# Revit family: ShowerTray_70x70cm_Vitra_ArkitektSeries_5735L003-0578
name_source: partatom
category: Plumbing Fixtures
revit_build: Autodesk Revit 2017 (Build: 20160225_1515(x64)
units: mm (PartAtom-declared; Revit-internal decimal feet)

## family parameters
Cut with Voids When Loaded = No
Host = Face
OmniClass Number = 23.45.05.14.17
OmniClass Title = Showers
Part Type = Normal
Room Calculation Point = No
Round Connector Dimension = Use Diameter
Shared = Yes

## types (1)
- ShowerTray_70x70cm_Vitra_ArkitektSeries_5735L003-0578
    Article No. (default) = 5735L003-0578
    BIMobject category = Sanitary - Shower trays
    Brand = Vitra
    CW Connection = No
    Color = White
    Cost = 0 $
    Default Elevation = 0 mm  [stored 0 ft]
    Description = Vitra - Shower Tray - 70x70 cm
    Design country = Turkey
    HW Connection = No
    IFC Classification = Sanitary Terminal
    Manufacturer = Vitra
    Manufacturer name = Vitra
    Masterformat 2014 Code = 22 41 23
    Masterformat 2014 Description = Residential Showers
    Model = 5735L003-0578
    MountingType = Floor Mounted
    NBS Referans Code = 35-06-84
    NBS Referans Description = Shower Trays
    Nominal Depth = 700 mm  [stored 2.29659 ft]
    NominalHeight = 75 mm  [stored 0.246063 ft]
    NominalWidth = 700 mm  [stored 2.29659 ft]
    OmniClass Code = 23-31 17 00
    OmniClass Description = Showers
    Product SKU = 5735L003-0578
    Product certification = https://vitraglobal.com
    Product family = Floor Mounted Shower Tray
    Product group = Arkitekt
    Secondary Material = White
    UNSPSC Code = 301815
    URL = https://vitraglobal.com
    Uniclass 1.4 Code = L7214
    Uniclass 1.4 Description = Showers
    Uniclass 2.0 Code = PR-35-06-84
    Uniclass 2.0 Description = Shower Trays
    Uniclass 2015 Code = Pr_40_20_06_84
    Uniclass 2015 Name = Shower trays
    Uniformat II Code = D2010
    Uniformat II Description = Plumbing Fixtures
    Vent Connection = No
    Warranty Period (Year) = 10 Years
    Waste Connection = Yes
    Weight Net (kg) = 25,668
    Youtube = https://www.youtube.com

note: [stored X ft] marks values corroborated as IEEE doubles in the binary element streams (Revit-internal decimal feet)

## geometry (parser evidence)
native form markers: Sweep x2
no freeform markers — native parametric forms only
